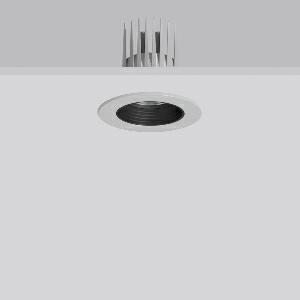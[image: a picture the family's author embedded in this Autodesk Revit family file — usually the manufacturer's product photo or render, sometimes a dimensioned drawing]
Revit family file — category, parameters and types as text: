
# Revit family: heledon_mini_e_901744_004_1_1ed2
name_source: partatom
category: Lighting Fixtures
units: mm (PartAtom-declared; Revit-internal decimal feet)

## family parameters
Cut with Voids When Loaded = No
Host = Face
Light Source = No
Part Type = Normal
Room Calculation Point = No
Round Connector Dimension = Use Diameter
Shared = No

## types (1)
- HELEDON mini E (1 x LED Modul 940, 2250 lm, 4000)
    Apparent Load = 20 VA
    Approval mark = CE
    CIE Flux Codes = 96 100 100 100 100
    Color Rendering = 92
    Color Temperature = 4000
    Default Elevation = 1800 mm
    Description = Series: HELEDON mini
Round recessed downlight. Housing: die-cast aluminium, powder-coated. Black plastic ring and recessed LED to prevent glare from the side. Optical assembly with lens made of plastic (polycarbonate) for the best homogeneous light distribution - can be changed without tools. Best colour rendering index Ra>90. Suitable for Recessed ceiling mounting. Installation without tools thanks to spring fastening system. Including separate LED converter with connecting cable 600 mm.High quality converter without flickering and stroboscopic effect. Through-wiring box (5 pole) available as accessory. The following accessories can be mounted without use of tools: interchangeable lenses, decorative glasses, honeycomb louvre, clear and frosted diffusers, white interchangeable plastic ring. 
Colour: silver
Diameter: 124 mm
Height: 3 mm
Cut-out diameter: 114 mm
Recess height: 170 mm
Luminaire: recess height: 120 mm
Lamp: LED
Socket: without socket
Colour temperature: 4000K
Colour rendering index (CRI): 92
System power: 20 W
Rated luminous flux: 2250 lm
Luminous efficiency: 113 lm/W
Control gear: Regulated power supply
Protection class: II
Type of protection: IP 20
    Height = 0 mm  [stored 0 ft]
    Lamp = 1 x LED Modul 940
    Lamp Light Flux = 2250 lm
    Lamp count = 1
    Length = 124 mm  [stored 0.406824 ft]
    Lifetime = 50000 h
    Luminous efficacy = 113 lm/W
    Manufacturer = RZB
    ModVariant = No
    Model = 901744.004.1
    Mounting Place = Ceiling
    Mounting Type = Recessed
    Number of Poles = 1
    OnlyDefault = Yes
    Power Factor = 1
    Product Name = HELEDON mini E
    Product group = Recessed downlights
    ProductGroupID = 402
    Protection Class = Protection class II
    Protection Degree = IP 20
    RLX_Detail_Level = 1
    RLX_Emergency_Light_Flux = 0 lm
    RLX_Emergency_Type = 0
    RLX_Emergency_Type_DB = No
    RlxData = <blob elided: 126337 chars, md5=7f6817df>
    Socket = socket
    Standby Power = 0 W
    System Light Flux = 2250 lm
    System Power = 20 W
    Type Comments = Product without accessories
    Type Image = 901656.004.jpg
    URL = http://relux.com
    VarID = ---
    Voltage = 230 V
    Voltage Range = 220-240 V
    Weight = 0.00 kg
    Width = 0 mm  [stored 0 ft]

note: [stored X ft] marks values corroborated as IEEE doubles in the binary element streams (Revit-internal decimal feet)

## geometry (parser evidence)
native form markers: Blend x4, Sweep x10
no freeform markers — native parametric forms only
